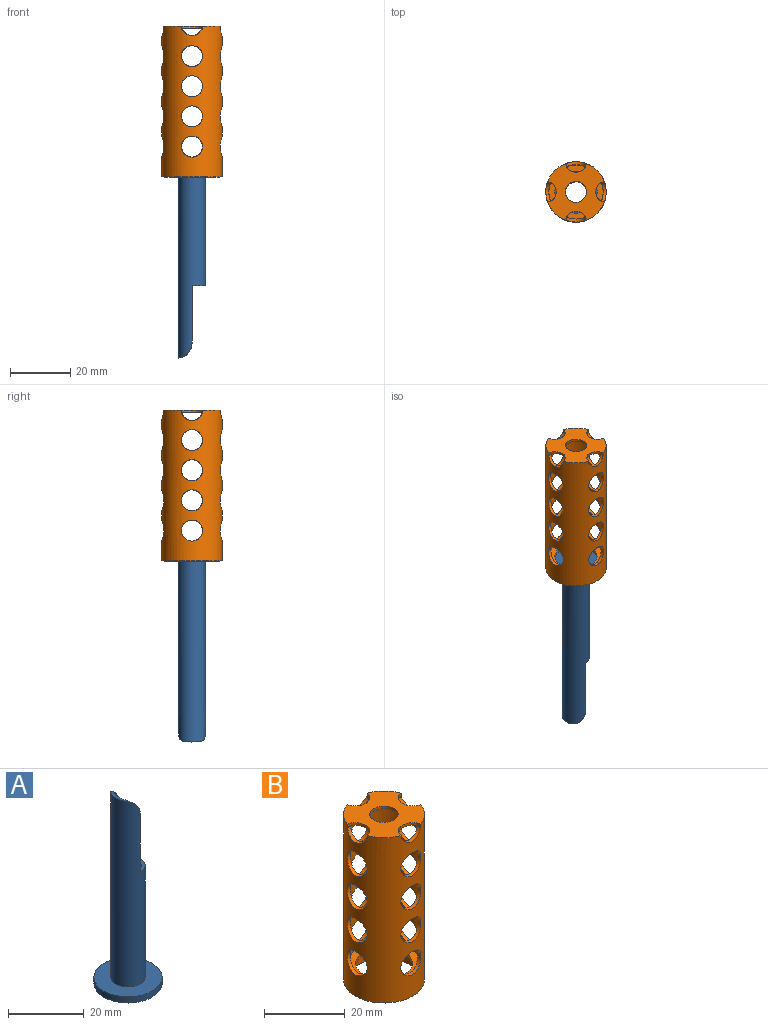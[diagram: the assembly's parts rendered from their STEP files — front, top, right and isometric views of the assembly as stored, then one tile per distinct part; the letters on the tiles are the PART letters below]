
ASSEMBLY  parts=2 mates=1
PART A: 9 faces, bbox 18x18x62 mm
  f0: cylinder r=3.5mm len=61.77mm, axis (0,0,-1), area 1087.3mm2, adj f4,f5,f6,f7,f8
  f1: cylinder r=4.5mm len=59.98mm, axis (0,0,-1), area 1345.6mm2, adj f3,f5,f6,f7,f8
  f2: cylinder r=8.97mm len=17.95mm, axis (0,0,-1), area 112.8mm2, adj f3,f4
  f3: plane 17.95x17.95mm, normal (0,0,1), area 189.4mm2, adj f1,f2
  f4: plane 17.95x17.95mm, normal (0,0,-1), area 214.6mm2, adj f0,f2
  f5: plane 9x4.5mm, normal (0,0,1), area 12.6mm2, adj f0,f1,f6,f7
  f6: plane 19x1mm, normal (1,0,0), area 19mm2, adj f0,f1,f5,f8
  f7: plane 19x1mm, normal (1,0,0), area 19mm2, adj f0,f1,f5,f8
  f8: cylinder r=5mm len=9mm, axis (0,1,0), area 18.6mm2, adj f0,f1,f6,f7
PART B: 42 faces, bbox 20x20x50 mm
  f0: cylinder r=9mm len=44.2mm, axis (0,0,-1), area 1820.8mm2, adj f1,f3,f4,f5,f6,f7,f8,f9
  f1: plane 18.4x17.7mm, normal (0,0,-1), area 172.4mm2, adj f0,f3,f4,f5,f6,f25,f28,f31
  f2: cylinder r=10mm len=50mm, axis (0,0,-1), area 2443.2mm2, adj f3,f4,f5,f6,f7,f8,f9,f10
  f3: cylinder r=3.5mm len=6.61mm, axis (0,-1,0), area 8.6mm2, adj f0,f1,f2,f35,f36,f37
  f4: cylinder r=3.5mm len=6.61mm, axis (0,-1,0), area 8.6mm2, adj f0,f1,f2,f32,f33,f34
  f5: cylinder r=3.5mm len=6.81mm, axis (-1,0,0), area 9.5mm2, adj f0,f1,f2,f29,f30,f31
  f6: cylinder r=3.5mm len=6.81mm, axis (-1,0,0), area 9.5mm2, adj f0,f1,f2,f26,f27,f28
  f7: cylinder r=3.5mm len=7mm, axis (0,-1,0), area 22.8mm2, adj f0,f2
  f8: cylinder r=3.5mm len=7mm, axis (0,-1,0), area 22.8mm2, adj f0,f2
  f9: cylinder r=3.5mm len=7mm, axis (0,-1,0), area 22.8mm2, adj f0,f2
  f10: cylinder r=3.5mm len=7mm, axis (0,-1,0), area 22.8mm2, adj f0,f2
  f11: plane 20x20mm, normal (0,0,-1), area 59.7mm2, adj f2,f39
  f12: cylinder r=3.5mm len=7mm, axis (0,-1,0), area 22.8mm2, adj f0,f2
  f13: cylinder r=3.5mm len=7mm, axis (0,-1,0), area 22.8mm2, adj f0,f2
  f14: cylinder r=3.5mm len=7mm, axis (0,-1,0), area 22.8mm2, adj f0,f2
  f15: cylinder r=3.5mm len=7mm, axis (0,-1,0), area 22.8mm2, adj f0,f2
  f16: cylinder r=3.5mm len=7mm, axis (-1,0,0), area 22.8mm2, adj f0,f2
  f17: cylinder r=3.5mm len=7mm, axis (-1,0,0), area 22.8mm2, adj f0,f2
  f18: cylinder r=3.5mm len=7mm, axis (-1,0,0), area 22.8mm2, adj f0,f2
  f19: cylinder r=3.5mm len=7mm, axis (-1,0,0), area 22.8mm2, adj f0,f2
  f20: cylinder r=3.5mm len=7mm, axis (-1,0,0), area 22.8mm2, adj f0,f2
  f21: cylinder r=3.5mm len=7mm, axis (-1,0,0), area 22.8mm2, adj f0,f2
  f22: cylinder r=3.5mm len=7mm, axis (-1,0,0), area 22.8mm2, adj f0,f2
  f23: cylinder r=3.5mm len=7mm, axis (-1,0,0), area 22.8mm2, adj f0,f2
  f24: plane 18.78x18.78mm, normal (0,0,1), area 204.4mm2, adj f2,f25,f28,f31,f34,f37
  f25: cylinder r=3.5mm len=7mm, axis (0,0,1), area 17.6mm2, adj f1,f24
  f26: plane 0.42x0.09mm, normal (0,0,1), area 0mm2, adj f2,f6,f28
  f27: plane 0.42x0.09mm, normal (0,0,1), area 0mm2, adj f2,f6,f28
  f28: cylinder r=3.5mm len=6.89mm, axis (0,0,1), area 7.9mm2, adj f1,f2,f6,f24,f26,f27
  f29: plane 0.42x0.09mm, normal (0,0,1), area 0mm2, adj f2,f5,f31
  f30: plane 0.42x0.09mm, normal (0,0,1), area 0mm2, adj f2,f5,f31
  f31: cylinder r=3.5mm len=6.89mm, axis (0,0,1), area 7.9mm2, adj f1,f2,f5,f24,f29,f30
  f32: plane 0.82x0.22mm, normal (0,0,1), area 0.1mm2, adj f2,f4,f34
  f33: plane 0.82x0.22mm, normal (0,0,1), area 0.1mm2, adj f2,f4,f34
  f34: cylinder r=3.5mm len=6.89mm, axis (0,0,1), area 8.1mm2, adj f1,f2,f4,f24,f32,f33
  f35: plane 0.82x0.22mm, normal (0,0,1), area 0.1mm2, adj f2,f3,f37
  f36: plane 0.82x0.22mm, normal (0,0,1), area 0.1mm2, adj f2,f3,f37
  f37: cylinder r=3.5mm len=6.89mm, axis (0,0,1), area 8.1mm2, adj f1,f2,f3,f24,f35,f36
  f38: plane 18x18mm, normal (0,0,1), area 100.5mm2, adj f0,f41
  f39: cylinder r=9mm len=18mm, axis (0,0,-1), area 226.2mm2, adj f11,f40
  f40: plane 18x18mm, normal (0,0,-1), area 100.5mm2, adj f39,f41
  f41: cylinder r=7mm len=14mm, axis (0,0,-1), area 44mm2, adj f38,f40
PLACE A rot(axis=(1,0,0),180deg) t=(-6.54,-7.42,-4.46)mm
PLACE B t=(-6.54,-7.42,-6.29)mm fixed
MATE slider B.f0 <-> A.f2  axis (0,0,-1) through (-6.54,-7.42,-2.29)mm
